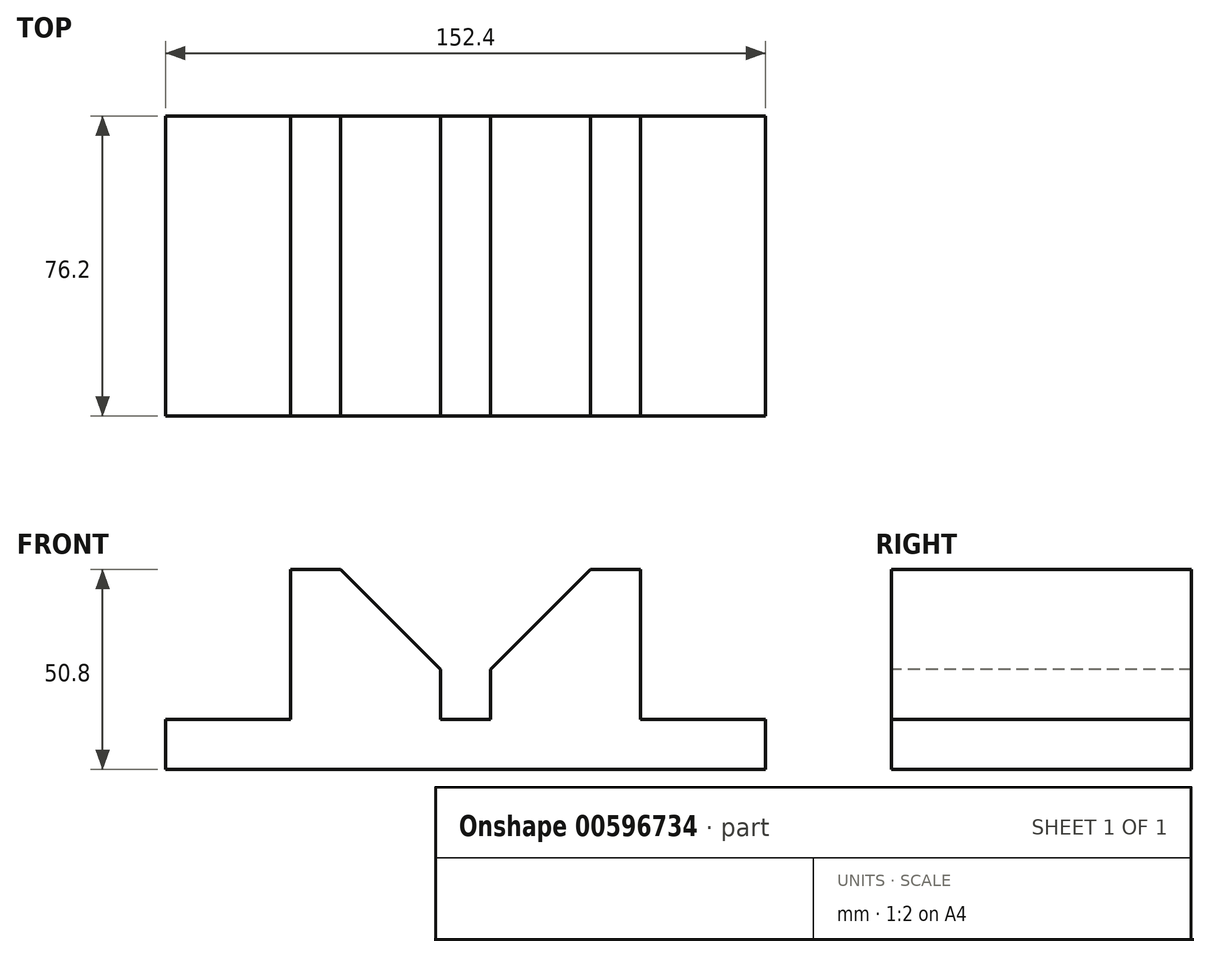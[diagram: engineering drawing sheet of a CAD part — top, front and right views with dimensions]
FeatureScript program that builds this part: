
annotation { "Feature Type Name" : "Feature", "Feature Type Description" : "" }
export const myFeature = defineFeature(function(context is Context, id is Id, definition is map)
    precondition{}
    {
        {
            var Q0;
            Q0=qCreatedBy(makeId("Top.planeOp"),FACE);
            var sketch = newSketch(context, id + "F0", { "sketchPlane" : qUnion([Q0])});
            skLineSegment(sketch, "E0.bottom", {"start": v(0, 0) * mm, "end": v(152.4, 0) * mm});
            skLineSegment(sketch, "E0.top", {"start": v(0, 76.2) * mm, "end": v(152.4, 76.2) * mm});
            skLineSegment(sketch, "E0.left", {"start": v(0, 0) * mm, "end": v(0, 76.2) * mm});
            skLineSegment(sketch, "E0.right", {"start": v(152.4, 0) * mm, "end": v(152.4, 76.2) * mm});
            skSolve(sketch);
        }
        {
            var Q0;
            Q0=makeQuery(id+"F0.imprint","IMPRINT",FACE,{"disambiguationData":[TD([[makeQuery(id+"F0.imprint","IMPRINT",EDGE,{"derivedFrom":sQuery(id+"F0.wireOp",EDGE,"E0.bottom")}),1.0]])]});
            extrude(context, id + "F1", {"entities" : qUnion([Q0]), "depth" : 12.7 * mm, "offsetDistance" : 25.4 * mm});
        }
        {
            var Q0;
            Q0=makeQuery(id+"F1.opExtrude","CAP_FACE",FACE,{"disambiguationData":[OSD([sQuery(id+"F0.wireOp",EDGE,"E0.bottom"),sQuery(id+"F0.wireOp",EDGE,"E0.top"),sQuery(id+"F0.wireOp",EDGE,"E0.left"),sQuery(id+"F0.wireOp",EDGE,"E0.right")])],"isStart":false});
            var sketch = newSketch(context, id + "F2", { "sketchPlane" : qUnion([Q0])});
            skLineSegment(sketch, "E1.left", {"start": v(82.55, 0) * mm, "end": v(82.55, 76.2) * mm});
            skLineSegment(sketch, "E1.right", {"start": v(69.85, 0) * mm, "end": v(69.85, 76.2) * mm});
            skLineSegment(sketch, "E2.bottom", {"start": v(82.55, 0) * mm, "end": v(120.65, 0) * mm});
            skLineSegment(sketch, "E2.top", {"start": v(82.55, 76.2) * mm, "end": v(120.65, 76.2) * mm});
            skLineSegment(sketch, "E2.right", {"start": v(120.65, 0) * mm, "end": v(120.65, 76.2) * mm});
            skLineSegment(sketch, "E3.bottom", {"start": v(31.75, 0) * mm, "end": v(69.85, 0) * mm});
            skLineSegment(sketch, "E3.top", {"start": v(31.75, 76.2) * mm, "end": v(69.85, 76.2) * mm});
            skLineSegment(sketch, "E3.left", {"start": v(31.75, 0) * mm, "end": v(31.75, 76.2) * mm});
            skSolve(sketch);
        }
        {
            var Q0;
            Q0=makeQuery(id+"F2.imprint","IMPRINT",FACE,{"disambiguationData":[TD([[makeQuery(id+"F2.imprint","IMPRINT",EDGE,{"derivedFrom":sQuery(id+"F2.wireOp",EDGE,"E3.bottom")}),1.0]])]});
            var Q1;
            Q1=makeQuery(id+"F2.imprint","IMPRINT",FACE,{"disambiguationData":[TD([[makeQuery(id+"F2.imprint","IMPRINT",EDGE,{"derivedFrom":sQuery(id+"F2.wireOp",EDGE,"E2.bottom")}),1.0]])]});
            extrude(context, id + "F3", {"entities" : qUnion([Q0, Q1]), "operationType" : NewBodyOperationType.ADD, "depth" : 38.1 * mm, "offsetDistance" : 25.4 * mm});
        }
        {
            var Q0;
            Q0=makeQuery(id+"F3.boolean.opBoolean","MERGE",FACE,{"derivedFrom":[makeQuery(id+"F1.opExtrude","SWEPT_FACE",FACE,{"disambiguationData":[OSD([sQuery(id+"F0.wireOp",EDGE,"E0.bottom")])]}),makeQuery(id+"F3.opExtrude","SWEPT_FACE",FACE,{"disambiguationData":[OSD([sQuery(id+"F2.wireOp",EDGE,"E2.bottom")])]}),makeQuery(id+"F3.opExtrude","SWEPT_FACE",FACE,{"disambiguationData":[OSD([sQuery(id+"F2.wireOp",EDGE,"E3.bottom")])]})]});
            var sketch = newSketch(context, id + "F4", { "sketchPlane" : qUnion([Q0])});
            skLineSegment(sketch, "E4", {"start": v(69.85, 50.8) * mm, "end": v(69.85, 25.4) * mm});
            skLineSegment(sketch, "E5", {"start": v(69.85, 50.8) * mm, "end": v(44.45, 50.8) * mm});
            skLineSegment(sketch, "E6", {"start": v(44.45, 50.8) * mm, "end": v(69.85, 25.4) * mm});
            skSolve(sketch);
        }
        {
            var Q0;
            Q0=makeQuery(id+"F4.imprint","IMPRINT",FACE,{"disambiguationData":[TD([[makeQuery(id+"F4.imprint","IMPRINT",EDGE,{"derivedFrom":sQuery(id+"F4.wireOp",EDGE,"E4")}),-1.0]])]});
            extrude(context, id + "F5", {"entities" : qUnion([Q0]), "operationType" : NewBodyOperationType.REMOVE, "oppositeDirection" : true, "depth" : 76.2 * mm, "offsetDistance" : 25.4 * mm});
        }
        {
            var Q0;
            Q0=makeQuery(id+"F3.boolean.opBoolean","MERGE",FACE,{"derivedFrom":[makeQuery(id+"F1.opExtrude","SWEPT_FACE",FACE,{"disambiguationData":[OSD([sQuery(id+"F0.wireOp",EDGE,"E0.bottom")])]}),makeQuery(id+"F3.opExtrude","SWEPT_FACE",FACE,{"disambiguationData":[OSD([sQuery(id+"F2.wireOp",EDGE,"E2.bottom")])]}),makeQuery(id+"F3.opExtrude","SWEPT_FACE",FACE,{"disambiguationData":[OSD([sQuery(id+"F2.wireOp",EDGE,"E3.bottom")])]})]});
            var sketch = newSketch(context, id + "F6", { "sketchPlane" : qUnion([Q0])});
            skLineSegment(sketch, "E7", {"start": v(82.55, 50.8) * mm, "end": v(107.95, 50.8) * mm});
            skLineSegment(sketch, "E8", {"start": v(82.55, 50.8) * mm, "end": v(82.55, 25.4) * mm});
            skLineSegment(sketch, "E9", {"start": v(82.55, 25.4) * mm, "end": v(107.95, 50.8) * mm});
            skSolve(sketch);
        }
        {
            var Q0;
            Q0=makeQuery(id+"F6.imprint","IMPRINT",FACE,{"disambiguationData":[TD([[makeQuery(id+"F6.imprint","IMPRINT",EDGE,{"derivedFrom":sQuery(id+"F6.wireOp",EDGE,"E7")}),-1.0]])]});
            extrude(context, id + "F7", {"entities" : qUnion([Q0]), "operationType" : NewBodyOperationType.REMOVE, "oppositeDirection" : true, "depth" : 76.2 * mm, "offsetDistance" : 25.4 * mm});
        }
    });
